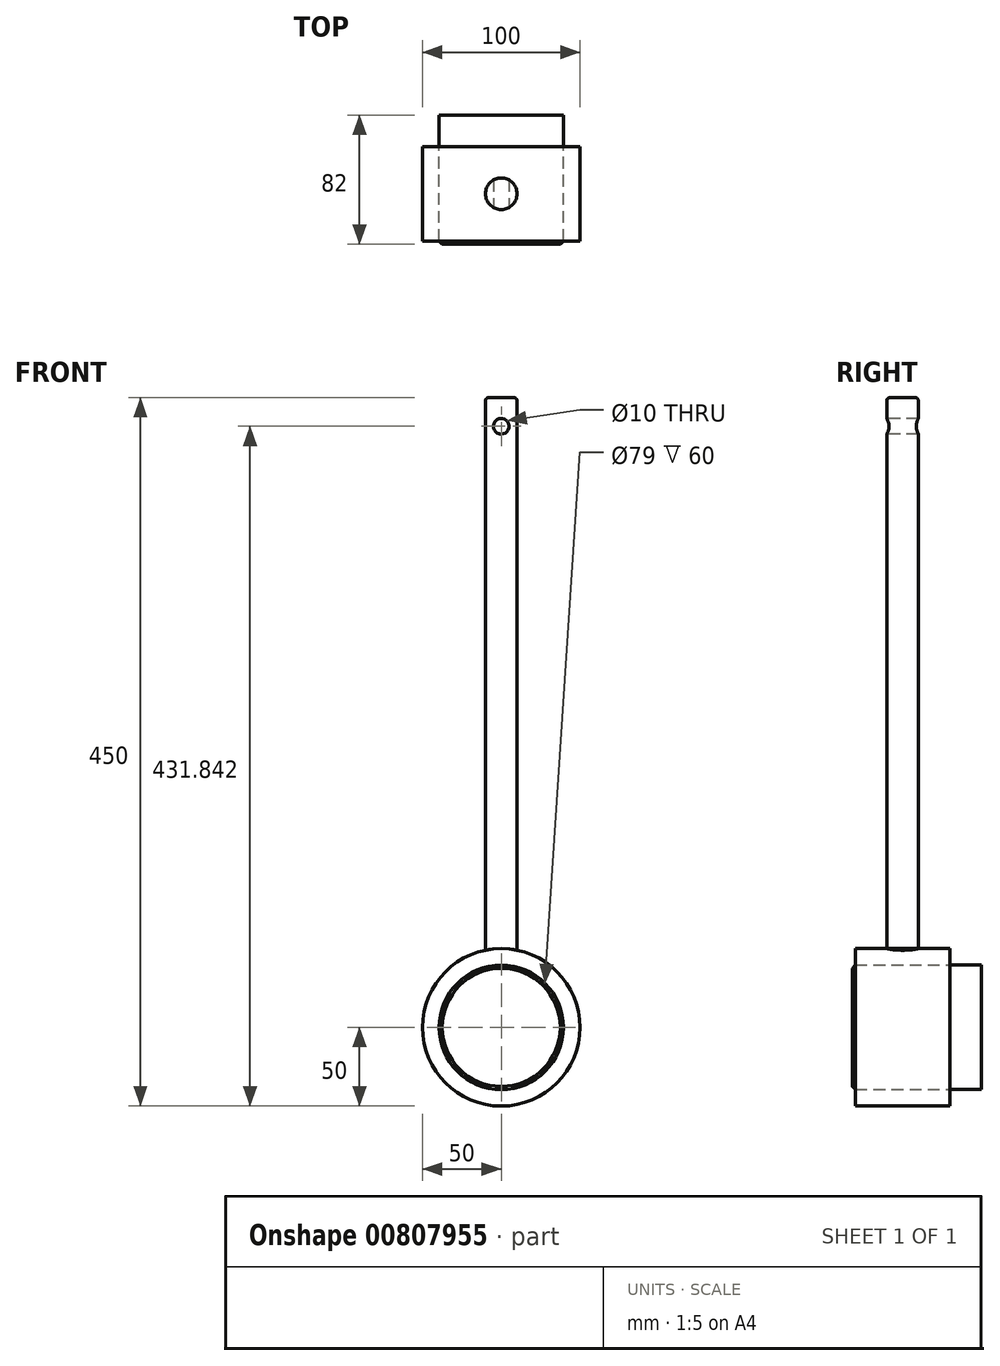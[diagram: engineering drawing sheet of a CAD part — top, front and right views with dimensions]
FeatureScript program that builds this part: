
annotation { "Feature Type Name" : "Feature", "Feature Type Description" : "" }
export const myFeature = defineFeature(function(context is Context, id is Id, definition is map)
    precondition{}
    {
        {
            var Q0;
            Q0=qCreatedBy(makeId("Front.planeOp"),FACE);
            var sketch = newSketch(context, id + "F0", { "sketchPlane" : qUnion([Q0])});
            skCircle(sketch, "E0", {"center": v(0, 0) * mm, "radius": 39.5 * mm});
            skCircle(sketch, "E1", {"center": v(0, 0) * mm, "radius": 50 * mm});
            skSolve(sketch);
        }
        {
            var Q0;
            Q0 = qSketchRegion(id + "F0", true);
            extrude(context, id + "F1", {"entities" : qUnion([Q0]), "depth" : 30 * mm, "offsetDistance" : 25 * mm, "hasSecondDirection" : true, "secondDirectionOppositeDirection" : true, "secondDirectionDepth" : 30 * mm});
        }
        {
            var Q0;
            Q0=makeQuery(id+"F1.opExtrude","CAP_FACE",FACE,{"disambiguationData":[OSD([sQuery(id+"F0.wireOp",EDGE,"E0"),sQuery(id+"F0.wireOp",EDGE,"E1")])],"isStart":false});
            var sketch = newSketch(context, id + "F2", { "sketchPlane" : qUnion([Q0])});
            skLineSegment(sketch, "E2", {"start": v(0, 50) * mm, "end": v(101.94, 50) * mm, "construction": true});
            skSolve(sketch);
        }
        {
            var Q0;
            Q0=qCreatedBy(makeId("Top.planeOp"),FACE);
            var Q1;
            Q1=sQuery(id+"F2.wireOp",VERTEX,"E2.start");
            cPlane(context, id + "F3", {"entities" : qUnion([Q0, Q1]), "cplaneType" : CPlaneType.PLANE_POINT, "offset" : 25 * mm, "width" : 150 * mm, "height" : 150 * mm});
        }
        {
            var Q0;
            Q0=qCreatedBy(id+"F3.planeOp",FACE);
            var sketch = newSketch(context, id + "F4", { "sketchPlane" : qUnion([Q0])});
            skCircle(sketch, "E3", {"center": v(0, 0) * mm, "radius": 10 * mm});
            skSolve(sketch);
        }
        {
            var Q0;
            Q0 = qSketchRegion(id + "F4", true);
            var Q1;
            Q1=makeQuery(id+"F1.opExtrude","SWEPT_FACE",FACE,{"disambiguationData":[OSD([sQuery(id+"F0.wireOp",EDGE,"E1")])]});
            extrude(context, id + "F5", {"entities" : qUnion([Q0]), "depth" : 350 * mm, "offsetDistance" : 25 * mm, "hasSecondDirection" : true, "secondDirectionBound" : SecondDirectionBoundingType.UP_TO_SURFACE, "secondDirectionOppositeDirection" : true, "secondDirectionDepth" : 25 * mm, "secondDirectionBoundEntityFace" : qUnion([Q1])});
        }
        {
            var Q0;
            Q0=qCreatedBy(makeId("Front.planeOp"),FACE);
            var sketch = newSketch(context, id + "F6", { "sketchPlane" : qUnion([Q0])});
            skCircle(sketch, "E4", {"center": v(0, 381.84) * mm, "radius": 5 * mm});
            skSolve(sketch);
        }
        {
            var Q0;
            Q0 = qSketchRegion(id + "F6", true);
            extrude(context, id + "F7", {"entities" : qUnion([Q0]), "operationType" : NewBodyOperationType.REMOVE, "oppositeDirection" : true, "depth" : 25 * mm, "offsetDistance" : 25 * mm, "hasSecondDirection" : true, "secondDirectionOppositeDirection" : false, "secondDirectionDepth" : 25 * mm});
        }
        {
            var Q0;
            Q0=qCreatedBy(makeId("Front.planeOp"),FACE);
            var sketch = newSketch(context, id + "F8", { "sketchPlane" : qUnion([Q0])});
            skCircle(sketch, "E5.0", {"center": v(0, 0) * mm, "radius": 39.5 * mm});
            skSolve(sketch);
        }
        {
            var Q0;
            Q0 = qSketchRegion(id + "F8", true);
            extrude(context, id + "F9", {"entities" : qUnion([Q0]), "depth" : 32 * mm, "offsetDistance" : 25 * mm, "hasSecondDirection" : true, "secondDirectionOppositeDirection" : true, "secondDirectionDepth" : 50 * mm});
        }
        {
            var Q0;
            Q0=makeQuery(id+"F9.opExtrude","CAP_EDGE",EDGE,{"disambiguationData":[OSD([sQuery(id+"F8.wireOp",EDGE,"E5.0")])],"isStart":false});
            chamfer(context, id + "F10", {"entities" : qUnion([Q0]), "chamferType" : ChamferType.OFFSET_ANGLE, "width" : 2 * mm, "oppositeDirection" : false, "angle" : 45 * degree, "tangentPropagation" : true});
        }
        {
            var Q0;
            {var subQ0=sQuery(id+"F4.wireOp",EDGE,"E3");Q0=makeQuery(id+"F5.opExtrude","CAP_EDGE",EDGE,{"disambiguationData":[OSD([subQ0]),topologyDisambiguationEdgeConnected([makeQuery(id+"F4.imprint","IMPRINT",EDGE,{"derivedFrom":subQ0})])],"isStart":false});}
            fillet(context, id + "F11", {"entities" : qUnion([Q0]), "radius" : 2 * mm, "tangentPropagation" : true, "allowEdgeOverflow" : false});
        }
    });
